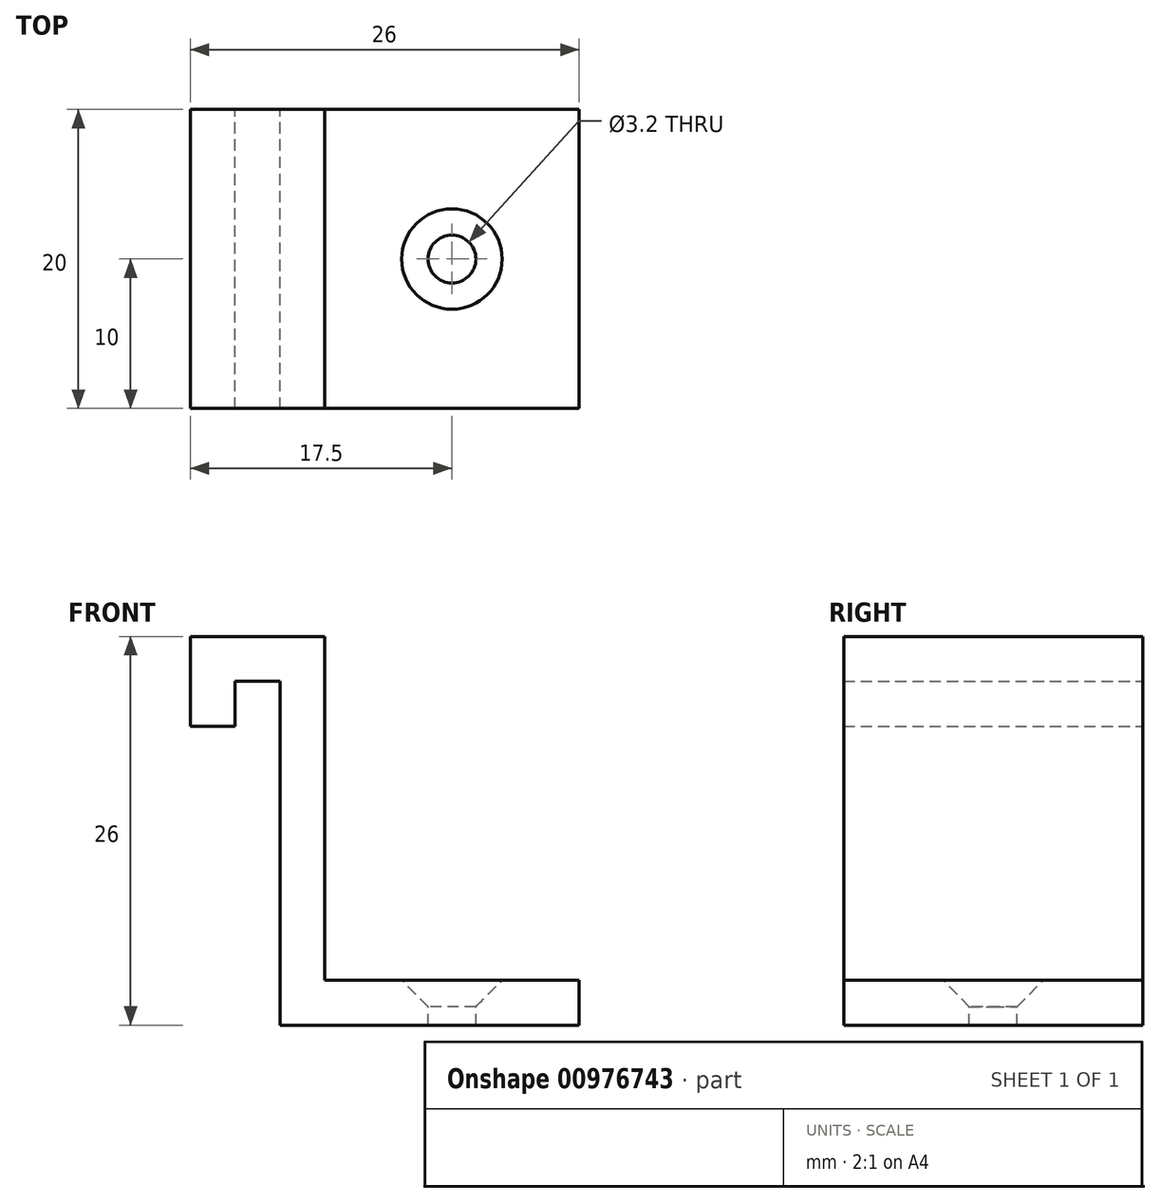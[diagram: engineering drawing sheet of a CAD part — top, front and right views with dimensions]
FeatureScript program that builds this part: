
annotation { "Feature Type Name" : "Feature", "Feature Type Description" : "" }
export const myFeature = defineFeature(function(context is Context, id is Id, definition is map)
    precondition{}
    {
        {
            var Q0;
            Q0=qCreatedBy(makeId("Front.planeOp"),FACE);
            var sketch = newSketch(context, id + "F0", { "sketchPlane" : qUnion([Q0])});
            skLineSegment(sketch, "E0", {"start": v(0, 0) * mm, "end": v(0, 23) * mm});
            skLineSegment(sketch, "E1", {"start": v(0, 23) * mm, "end": v(-3, 23) * mm});
            skLineSegment(sketch, "E2", {"start": v(-3, 23) * mm, "end": v(-3, 20) * mm});
            skLineSegment(sketch, "E3", {"start": v(-3, 20) * mm, "end": v(-6, 20) * mm});
            skLineSegment(sketch, "E4", {"start": v(-6, 20) * mm, "end": v(-6, 26) * mm});
            skLineSegment(sketch, "E5", {"start": v(-6, 26) * mm, "end": v(3, 26) * mm});
            skLineSegment(sketch, "E6", {"start": v(3, 26) * mm, "end": v(3, 3) * mm});
            skLineSegment(sketch, "E7", {"start": v(3, 3) * mm, "end": v(20, 3) * mm});
            skLineSegment(sketch, "E8", {"start": v(20, 3) * mm, "end": v(20, 0) * mm});
            skLineSegment(sketch, "E9", {"start": v(20, 0) * mm, "end": v(0, 0) * mm});
            skSolve(sketch);
        }
        {
            var Q0;
            Q0=makeQuery(id+"F0.imprint","IMPRINT",FACE,{"disambiguationData":[TD([[makeQuery(id+"F0.imprint","IMPRINT",EDGE,{"derivedFrom":sQuery(id+"F0.wireOp",EDGE,"E0")}),-1.0]])]});
            extrude(context, id + "F1", {"entities" : qUnion([Q0]), "depth" : 20 * mm, "offsetDistance" : 25 * mm});
        }
        {
            var Q0;
            Q0=makeQuery(id+"F1.opExtrude","SWEPT_FACE",FACE,{"disambiguationData":[OSD([sQuery(id+"F0.wireOp",EDGE,"E7")])]});
            var sketch = newSketch(context, id + "F2", { "sketchPlane" : qUnion([Q0])});
            skLineSegment(sketch, "E10", {"start": v(3, -20) * mm, "end": v(20, 0) * mm});
            skPoint(sketch, "E11", {"position": v(11.5, -10) * mm});
            skSolve(sketch);
        }
        {
            var Q0;
            Q0=sQuery(id+"F2.wireOp",VERTEX,"E11");
            var Q1;
            Q1=makeQuery(id+"F1.opExtrude","SWEPT_BODY",BODY,{"disambiguationData":[OSD([sQuery(id+"F0.wireOp",EDGE,"E0"),sQuery(id+"F0.wireOp",EDGE,"E1"),sQuery(id+"F0.wireOp",EDGE,"E2"),sQuery(id+"F0.wireOp",EDGE,"E3"),sQuery(id+"F0.wireOp",EDGE,"E4"),sQuery(id+"F0.wireOp",EDGE,"E5"),sQuery(id+"F0.wireOp",EDGE,"E6"),sQuery(id+"F0.wireOp",EDGE,"E7"),sQuery(id+"F0.wireOp",EDGE,"E8"),sQuery(id+"F0.wireOp",EDGE,"E9")])]});
            hole(context, id + "F3", {"style" : HoleStyle.C_SINK, "endStyle" : HoleEndStyle.THROUGH, "standardTappedOrClearance" : lookupTablePath({ "fit" : "Close", "standard" : "ISO", "size" : "M3", "type" : "Clearance" }), "standardBlindInLast" : lookupTablePath({ "fit" : "Close", "standard" : "ISO", "engagement" : "75%", "pitch" : "0.5 mm", "size" : "M3", "type" : "Clearance & tapped" }), "holeDiameter" : 3.2 * mm, "cSinkDiameter" : 6.72 * mm, "cSinkAngle" : 90 * degree, "majorDiameter" : 5 * mm, "isTappedThrough" : true, "tappedDepth" : 12 * mm, "tapClearance" : 3, "locations" : qUnion([Q0]), "scope" : qUnion([Q1])});
        }
    });
